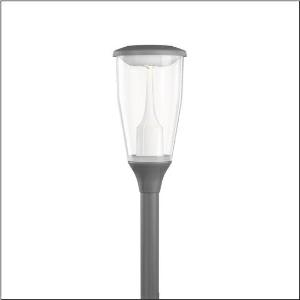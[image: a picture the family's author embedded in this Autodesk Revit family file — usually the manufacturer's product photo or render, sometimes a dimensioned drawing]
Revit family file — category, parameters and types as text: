
# Revit family: dl_11_iq___p1_0a_5xa5565lf14h000022_286d
name_source: partatom
category: Lighting Fixtures
units: mm (PartAtom-declared; Revit-internal decimal feet)

## family parameters
Cut with Voids When Loaded = No
Host = Face
Light Source = No
Part Type = Normal
Room Calculation Point = No
Round Connector Dimension = Use Diameter
Shared = No

## types (1)
- --- (1 x LED, 1530 lm, 10 W, 4000K)
    Apparent Load = 10 VA
    CIE Flux Codes = 34 63 91 95 100
    Color Rendering = 70
    Color Temperature = 4000K
    Default Elevation = 1800 mm
    Description = DL 11 iQ, mast luminaire, Module 540 iQ-SR, primary light control with 3 zone facetted reflector, of plastic, silver coated, highly specular, structured, primary optical cover: cover, of PMMA, transparent, light distribution: P1.0a, light emission: direct distribution, primary light characteristic: asymmetric, installation type: post-top, LED, High Power LED, rated luminous flux: 1.560lm, luminous efficacy: 149lm/W, light colour: 740, colour temperature: 4000K, control: Street-Remote, Auto-Match, Temp-Guard, Lumen-Switch, Night-Set, Smart-Wire, Light-Fading, Desk-Remote (wireless, voltage-free reading and setting of iQ features in the workshop via application-optimized NFC function/RFID function), optimised constant luminous flux control (CLO 2.0), mains connection: 220..240V, AC, 50/60Hz, connection cable pre-assembled, cable length: 5,5m, start of lifetime: 10W, end of service life: 10W, reduction: 5W, luminaire housing, upper part, of diecast aluminium, coated, Siteco® metallic grey (DB 702S), spigot size: 60mm (post-top), post-top mast mounting element, of diecast aluminium, coated, Siteco® metallic grey (DB 702S), Module 540 iQ-SR, traffic white (RAL 9016), equipment: standard, protection rating (complete): IP66, insulation class (complete): insulation class II (safety insulation), certification: CE, ENEC, ENEC+, VDE, packaging unit: 1 piece

Light Distribution: P1.0a
    Height = 665 mm
    Lamp = 1 x LED
    Lamp Light Flux = 1530 lm
    Lamp Power = 10 W
    Lamp count = 1
    Length = 334 mm
    Luminous efficacy = 153 lm/W
    Manufacturer = Siteco
    ModVariant = No
    Model = 5XA5565LF14H000022
    Number of Poles = 1
    OnlyDefault = Yes
    Power Factor = 1
    Product Name = DL 11 iQ | P1.0a
    Product group = mast luminaire | pylon top
    ProductGroupID = 6100
    Protection Class = Protection class II
    Protection Degree = IP 66
    RLX_Detail_Level = 1
    RLX_Emergency_Light_Flux = 0 lm
    RLX_Emergency_Type = 0
    RLX_Emergency_Type_DB = No
    RlxData = <blob elided: 107929 chars, md5=a07146b0>
    Socket = socket
    Standby Power = 0 W
    System Light Flux = 1530 lm
    System Power = 10 W
    Type Comments = factory setting: luminous flux: 100 % | dim-lin: 254 | 401 mA
    Type Image = l_1258354.jpg
    URL = http://relux.com
    VarID = @adj_060633
    Voltage = 0 V
    Weight = 0.00 kg
    Width = 0 mm  [stored 0 ft]

note: [stored X ft] marks values corroborated as IEEE doubles in the binary element streams (Revit-internal decimal feet)

## geometry (parser evidence)
native form markers: Blend x4, Sweep x9
no freeform markers — native parametric forms only
